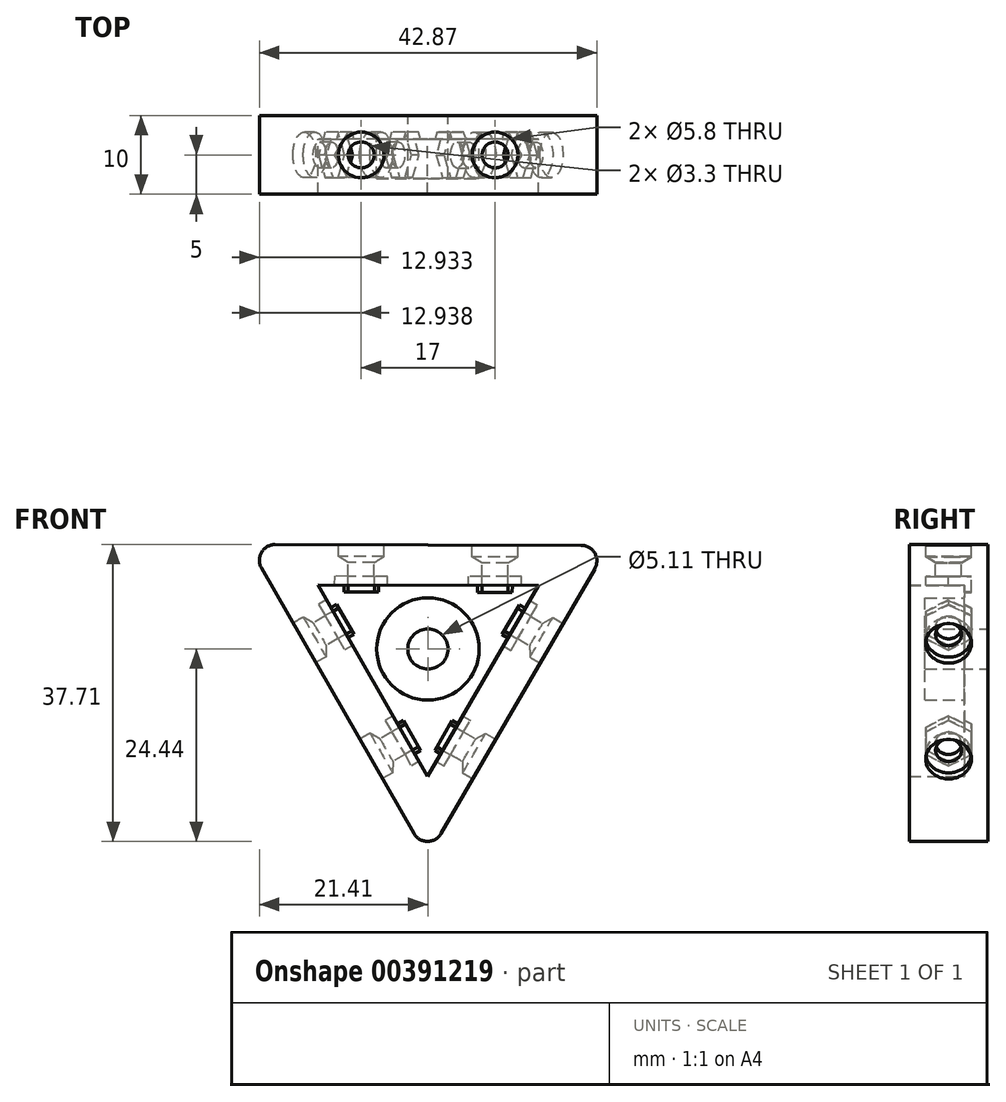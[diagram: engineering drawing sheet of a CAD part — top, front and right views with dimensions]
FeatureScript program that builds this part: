
annotation { "Feature Type Name" : "Feature", "Feature Type Description" : "" }
export const myFeature = defineFeature(function(context is Context, id is Id, definition is map)
    precondition{}
    {
        {
            var Q0;
            Q0=qCreatedBy(makeId("Front.planeOp"),FACE);
            var sketch = newSketch(context, id + "F0", { "sketchPlane" : qUnion([Q0])});
            skCircle(sketch, "E0.cCircle", {"center": v(0, 0) * mm, "radius": 13.22 * mm, "construction": true});
            skLineSegment(sketch, "E0.0", {"start": v(22.93, 13.17) * mm, "end": v(-0.06, -26.44) * mm});
            skLineSegment(sketch, "E0.1", {"start": v(-0.06, -26.44) * mm, "end": v(-22.87, 13.27) * mm});
            skLineSegment(sketch, "E0.2", {"start": v(-22.87, 13.27) * mm, "end": v(22.93, 13.17) * mm});
            skCircle(sketch, "E1.cCircle", {"center": v(0, 0) * mm, "radius": 8.08 * mm, "construction": true});
            skLineSegment(sketch, "E1.0", {"start": v(14.02, 8.05) * mm, "end": v(-0.04, -16.17) * mm});
            skLineSegment(sketch, "E1.1", {"start": v(-0.04, -16.17) * mm, "end": v(-13.98, 8.11) * mm});
            skLineSegment(sketch, "E1.2", {"start": v(-13.98, 8.11) * mm, "end": v(14.02, 8.05) * mm});
            skPoint(sketch, "E1.0.midPoint", {"position": v(7, -4.06) * mm});
            skPoint(sketch, "E2", {"position": v(2.72, -11.4) * mm});
            skPoint(sketch, "E3", {"position": v(11.26, 3.3) * mm});
            skPoint(sketch, "E4", {"position": v(8.52, 8.06) * mm});
            skPoint(sketch, "E5", {"position": v(-8.48, 8.1) * mm});
            skPoint(sketch, "E6", {"position": v(-10.82, 2.61) * mm});
            skPoint(sketch, "E7", {"position": v(-2.78, -11.4) * mm});
            skCircle(sketch, "E8", {"center": v(0, 0) * mm, "radius": 6.5 * mm});
            skSolve(sketch);
        }
        {
            var Q0;
            Q0=makeQuery(id+"F0.imprint","IMPRINT",FACE,{"disambiguationData":[TD([[makeQuery(id+"F0.imprint","IMPRINT",EDGE,{"derivedFrom":sQuery(id+"F0.wireOp",EDGE,"E1.0")}),-1.0]])]});
            extrude(context, id + "F1", {"entities" : qUnion([Q0]), "depth" : 3 * mm});
        }
        {
            var Q0;
            Q0=makeQuery(id+"F0.imprint","IMPRINT",FACE,{"disambiguationData":[TD([[makeQuery(id+"F0.imprint","IMPRINT",EDGE,{"derivedFrom":sQuery(id+"F0.wireOp",EDGE,"E0.0")}),-1.0]])]});
            extrude(context, id + "F2", {"entities" : qUnion([Q0]), "operationType" : NewBodyOperationType.ADD, "depth" : 10 * mm});
        }
        {
            var Q0;
            Q0=makeQuery(id+"F2.opExtrude","SWEPT_FACE",FACE,{"disambiguationData":[OSD([sQuery(id+"F0.wireOp",EDGE,"E0.0")])]});
            var sketch = newSketch(context, id + "F3", { "sketchPlane" : qUnion([Q0])});
            skPoint(sketch, "E9", {"position": v(-5, -8.5) * mm});
            skPoint(sketch, "E10", {"position": v(-5, 8.5) * mm});
            skPoint(sketch, "E10.positionSnap0", {"position": v(-5, 22.9) * mm});
            skCircle(sketch, "E11.cCircle", {"center": v(-5, -8.5) * mm, "radius": 2.9 * mm, "construction": true});
            skLineSegment(sketch, "E11.0", {"start": v(-2.1, -6.83) * mm, "end": v(-2.1, -10.17) * mm});
            skLineSegment(sketch, "E11.1", {"start": v(-2.1, -10.17) * mm, "end": v(-5, -11.85) * mm});
            skLineSegment(sketch, "E11.2", {"start": v(-5, -11.85) * mm, "end": v(-7.9, -10.17) * mm});
            skLineSegment(sketch, "E11.3", {"start": v(-7.9, -10.17) * mm, "end": v(-7.9, -6.83) * mm});
            skLineSegment(sketch, "E11.4", {"start": v(-7.9, -6.83) * mm, "end": v(-5, -5.15) * mm});
            skLineSegment(sketch, "E11.5", {"start": v(-5, -5.15) * mm, "end": v(-2.1, -6.83) * mm});
            skPoint(sketch, "E11.0.midPoint", {"position": v(-2.1, -8.5) * mm});
            skCircle(sketch, "E12.cCircle", {"center": v(-5, 8.5) * mm, "radius": 2.9 * mm, "construction": true});
            skLineSegment(sketch, "E12.0", {"start": v(-2.1, 10.17) * mm, "end": v(-2.1, 6.83) * mm});
            skLineSegment(sketch, "E12.1", {"start": v(-2.1, 6.83) * mm, "end": v(-5, 5.15) * mm});
            skLineSegment(sketch, "E12.2", {"start": v(-5, 5.15) * mm, "end": v(-7.9, 6.83) * mm});
            skLineSegment(sketch, "E12.3", {"start": v(-7.9, 6.83) * mm, "end": v(-7.9, 10.17) * mm});
            skLineSegment(sketch, "E12.4", {"start": v(-7.9, 10.17) * mm, "end": v(-5, 11.85) * mm});
            skLineSegment(sketch, "E12.5", {"start": v(-5, 11.85) * mm, "end": v(-2.1, 10.17) * mm});
            skPoint(sketch, "E12.0.midPoint", {"position": v(-2.1, 8.5) * mm});
            skSolve(sketch);
        }
        {
            var Q0;
            Q0=sQuery(id+"F3.wireOp",VERTEX,"E9");
            var Q1;
            Q1=sQuery(id+"F3.wireOp",VERTEX,"E10");
            var Q2;
            Q2=makeQuery(id+"F1.opExtrude","SWEPT_BODY",BODY,{"disambiguationData":[OSD([sQuery(id+"F0.wireOp",EDGE,"E1.0"),sQuery(id+"F0.wireOp",EDGE,"E1.1"),sQuery(id+"F0.wireOp",EDGE,"E1.2")])]});
            hole(context, id + "F4", {"style" : HoleStyle.SIMPLE, "endStyle" : HoleEndStyle.BLIND, "standardTappedOrClearance" : lookupTablePath({ "standard" : "ISO", "fit" : "Normal", "size" : "M3", "type" : "Clearance" }), "standardBlindInLast" : lookupTablePath({ "fit" : "Standard", "standard" : "ISO", "size" : "M3", "type" : "Clearance" }), "holeDiameter" : 3.3 * mm, "holeDepth" : 8 * mm, "tappedDepth" : 12 * mm, "tapClearance" : 3, "locations" : qUnion([Q0, Q1]), "scope" : qUnion([Q2])});
        }
        {
            var Q0;
            Q0=sQuery(id+"F3.wireOp",VERTEX,"E9");
            var Q1;
            Q1=sQuery(id+"F3.wireOp",VERTEX,"E10");
            var Q2;
            Q2=makeQuery(id+"F1.opExtrude","SWEPT_BODY",BODY,{"disambiguationData":[OSD([sQuery(id+"F0.wireOp",EDGE,"E1.0"),sQuery(id+"F0.wireOp",EDGE,"E1.1"),sQuery(id+"F0.wireOp",EDGE,"E1.2")])]});
            hole(context, id + "F5", {"style" : HoleStyle.SIMPLE, "endStyle" : HoleEndStyle.BLIND, "holeDiameter" : 5.8 * mm, "holeDepth" : 1.5 * mm, "tappedDepth" : 12 * mm, "tapClearance" : 3, "locations" : qUnion([Q0, Q1]), "scope" : qUnion([Q2])});
        }
        {
            var Q0;
            Q0=qSketchRegion(id+"F3",true);
            extrude(context, id + "F6", {"entities" : qUnion([Q0]), "operationType" : NewBodyOperationType.REMOVE, "oppositeDirection" : true, "depth" : 6 * mm, "hasSecondDirection" : true, "secondDirectionOppositeDirection" : true, "secondDirectionDepth" : 4 * mm});
        }
        {
            var Q0;
            Q0=makeQuery(id+"F2.opExtrude","SWEPT_FACE",FACE,{"disambiguationData":[OSD([sQuery(id+"F0.wireOp",EDGE,"E0.2")])]});
            var sketch = newSketch(context, id + "F7", { "sketchPlane" : qUnion([Q0])});
            skPoint(sketch, "E13", {"position": v(22.9, -5) * mm});
            skPoint(sketch, "E14", {"position": v(8.5, -5) * mm});
            skPoint(sketch, "E15", {"position": v(-8.5, -5) * mm});
            skPoint(sketch, "E15.positionSnap0", {"position": v(-22.9, -5) * mm});
            skCircle(sketch, "E16.cCircle", {"center": v(8.5, -5) * mm, "radius": 2.9 * mm, "construction": true});
            skLineSegment(sketch, "E16.0", {"start": v(5.15, -5) * mm, "end": v(6.83, -2.1) * mm});
            skLineSegment(sketch, "E16.1", {"start": v(6.83, -2.1) * mm, "end": v(10.17, -2.1) * mm});
            skLineSegment(sketch, "E16.2", {"start": v(10.17, -2.1) * mm, "end": v(11.85, -5) * mm});
            skLineSegment(sketch, "E16.3", {"start": v(11.85, -5) * mm, "end": v(10.17, -7.9) * mm});
            skLineSegment(sketch, "E16.4", {"start": v(10.17, -7.9) * mm, "end": v(6.83, -7.9) * mm});
            skLineSegment(sketch, "E16.5", {"start": v(6.83, -7.9) * mm, "end": v(5.15, -5) * mm});
            skPoint(sketch, "E16.0.midPoint", {"position": v(5.99, -3.55) * mm});
            skCircle(sketch, "E17.cCircle", {"center": v(-8.5, -5) * mm, "radius": 2.9 * mm, "construction": true});
            skLineSegment(sketch, "E17.0", {"start": v(-11.85, -5) * mm, "end": v(-10.17, -2.1) * mm});
            skLineSegment(sketch, "E17.1", {"start": v(-10.17, -2.1) * mm, "end": v(-6.83, -2.1) * mm});
            skLineSegment(sketch, "E17.2", {"start": v(-6.83, -2.1) * mm, "end": v(-5.15, -5) * mm});
            skLineSegment(sketch, "E17.3", {"start": v(-5.15, -5) * mm, "end": v(-6.83, -7.9) * mm});
            skLineSegment(sketch, "E17.4", {"start": v(-6.83, -7.9) * mm, "end": v(-10.17, -7.9) * mm});
            skLineSegment(sketch, "E17.5", {"start": v(-10.17, -7.9) * mm, "end": v(-11.85, -5) * mm});
            skPoint(sketch, "E17.0.midPoint", {"position": v(-11.01, -3.55) * mm});
            skSolve(sketch);
        }
        {
            var Q0;
            Q0=qSketchRegion(id+"F7",true);
            extrude(context, id + "F8", {"entities" : qUnion([Q0]), "operationType" : NewBodyOperationType.REMOVE, "oppositeDirection" : true, "depth" : 6 * mm, "hasSecondDirection" : true, "secondDirectionOppositeDirection" : true, "secondDirectionDepth" : 4 * mm});
        }
        {
            var Q0;
            Q0=sQuery(id+"F7.wireOp",VERTEX,"E14");
            var Q1;
            Q1=sQuery(id+"F7.wireOp",VERTEX,"E15");
            var Q2;
            Q2=makeQuery(id+"F1.opExtrude","SWEPT_BODY",BODY,{"disambiguationData":[OSD([sQuery(id+"F0.wireOp",EDGE,"E1.0"),sQuery(id+"F0.wireOp",EDGE,"E1.1"),sQuery(id+"F0.wireOp",EDGE,"E1.2")])]});
            hole(context, id + "F9", {"style" : HoleStyle.SIMPLE, "endStyle" : HoleEndStyle.BLIND, "holeDiameter" : 5.8 * mm, "holeDepth" : 1.5 * mm, "tappedDepth" : 12 * mm, "tapClearance" : 3, "locations" : qUnion([Q0, Q1]), "scope" : qUnion([Q2])});
        }
        {
            var Q0;
            Q0=sQuery(id+"F7.wireOp",VERTEX,"E14");
            var Q1;
            Q1=sQuery(id+"F7.wireOp",VERTEX,"E15");
            var Q2;
            Q2=makeQuery(id+"F1.opExtrude","SWEPT_BODY",BODY,{"disambiguationData":[OSD([sQuery(id+"F0.wireOp",EDGE,"E1.0"),sQuery(id+"F0.wireOp",EDGE,"E1.1"),sQuery(id+"F0.wireOp",EDGE,"E1.2")])]});
            hole(context, id + "F10", {"style" : HoleStyle.SIMPLE, "endStyle" : HoleEndStyle.BLIND, "standardTappedOrClearance" : lookupTablePath({ "standard" : "ISO", "fit" : "Normal", "size" : "M3", "type" : "Clearance" }), "standardBlindInLast" : lookupTablePath({ "fit" : "Standard", "standard" : "ISO", "size" : "M3", "type" : "Clearance" }), "holeDiameter" : 3.3 * mm, "holeDepth" : 8 * mm, "tappedDepth" : 12 * mm, "tapClearance" : 3, "locations" : qUnion([Q0, Q1]), "scope" : qUnion([Q2])});
        }
        {
            var Q0;
            Q0=makeQuery(id+"F2.opExtrude","SWEPT_FACE",FACE,{"disambiguationData":[OSD([sQuery(id+"F0.wireOp",EDGE,"E0.1")])]});
            var sketch = newSketch(context, id + "F11", { "sketchPlane" : qUnion([Q0])});
            skPoint(sketch, "E18", {"position": v(5, 8.5) * mm});
            skPoint(sketch, "E18.positionSnap0", {"position": v(5, 22.9) * mm});
            skPoint(sketch, "E19", {"position": v(5, -8.5) * mm});
            skPoint(sketch, "E19.positionSnap0", {"position": v(5, -22.9) * mm});
            skCircle(sketch, "E20.cCircle", {"center": v(5, 8.5) * mm, "radius": 2.9 * mm, "construction": true});
            skLineSegment(sketch, "E20.0", {"start": v(5, 5.15) * mm, "end": v(2.1, 6.83) * mm});
            skLineSegment(sketch, "E20.1", {"start": v(2.1, 6.83) * mm, "end": v(2.1, 10.17) * mm});
            skLineSegment(sketch, "E20.2", {"start": v(2.1, 10.17) * mm, "end": v(5, 11.85) * mm});
            skLineSegment(sketch, "E20.3", {"start": v(5, 11.85) * mm, "end": v(7.9, 10.17) * mm});
            skLineSegment(sketch, "E20.4", {"start": v(7.9, 10.17) * mm, "end": v(7.9, 6.83) * mm});
            skLineSegment(sketch, "E20.5", {"start": v(7.9, 6.83) * mm, "end": v(5, 5.15) * mm});
            skPoint(sketch, "E20.0.midPoint", {"position": v(3.55, 5.99) * mm});
            skCircle(sketch, "E21.cCircle", {"center": v(5, -8.5) * mm, "radius": 2.9 * mm, "construction": true});
            skLineSegment(sketch, "E21.0", {"start": v(5, -11.85) * mm, "end": v(2.1, -10.17) * mm});
            skLineSegment(sketch, "E21.1", {"start": v(2.1, -10.17) * mm, "end": v(2.1, -6.83) * mm});
            skLineSegment(sketch, "E21.2", {"start": v(2.1, -6.83) * mm, "end": v(5, -5.15) * mm});
            skLineSegment(sketch, "E21.3", {"start": v(5, -5.15) * mm, "end": v(7.9, -6.83) * mm});
            skLineSegment(sketch, "E21.4", {"start": v(7.9, -6.83) * mm, "end": v(7.9, -10.17) * mm});
            skLineSegment(sketch, "E21.5", {"start": v(7.9, -10.17) * mm, "end": v(5, -11.85) * mm});
            skPoint(sketch, "E21.0.midPoint", {"position": v(3.55, -11.01) * mm});
            skSolve(sketch);
        }
        {
            var Q0;
            Q0=qSketchRegion(id+"F11",true);
            extrude(context, id + "F12", {"entities" : qUnion([Q0]), "operationType" : NewBodyOperationType.REMOVE, "oppositeDirection" : true, "depth" : 6 * mm, "hasSecondDirection" : true, "secondDirectionOppositeDirection" : true, "secondDirectionDepth" : 4 * mm});
        }
        {
            var Q0;
            Q0=sQuery(id+"F11.wireOp",VERTEX,"E18");
            var Q1;
            Q1=sQuery(id+"F11.wireOp",VERTEX,"E19");
            var Q2;
            Q2=makeQuery(id+"F1.opExtrude","SWEPT_BODY",BODY,{"disambiguationData":[OSD([sQuery(id+"F0.wireOp",EDGE,"E1.0"),sQuery(id+"F0.wireOp",EDGE,"E1.1"),sQuery(id+"F0.wireOp",EDGE,"E1.2")])]});
            hole(context, id + "F13", {"style" : HoleStyle.SIMPLE, "endStyle" : HoleEndStyle.BLIND, "standardTappedOrClearance" : lookupTablePath({ "standard" : "ISO", "fit" : "Normal", "size" : "M3", "type" : "Clearance" }), "standardBlindInLast" : lookupTablePath({ "fit" : "Standard", "standard" : "ISO", "size" : "M3", "type" : "Clearance" }), "holeDiameter" : 3.3 * mm, "holeDepth" : 8 * mm, "tappedDepth" : 12 * mm, "tapClearance" : 3, "locations" : qUnion([Q0, Q1]), "scope" : qUnion([Q2])});
        }
        {
            var Q0;
            Q0=sQuery(id+"F11.wireOp",VERTEX,"E18");
            var Q1;
            Q1=sQuery(id+"F11.wireOp",VERTEX,"E19");
            var Q2;
            Q2=makeQuery(id+"F1.opExtrude","SWEPT_BODY",BODY,{"disambiguationData":[OSD([sQuery(id+"F0.wireOp",EDGE,"E1.0"),sQuery(id+"F0.wireOp",EDGE,"E1.1"),sQuery(id+"F0.wireOp",EDGE,"E1.2")])]});
            hole(context, id + "F14", {"style" : HoleStyle.SIMPLE, "endStyle" : HoleEndStyle.BLIND, "holeDiameter" : 5.8 * mm, "holeDepth" : 1.5 * mm, "tappedDepth" : 12 * mm, "tapClearance" : 3, "locations" : qUnion([Q0, Q1]), "scope" : qUnion([Q2])});
        }
        {
            var Q0;
            Q0=makeQuery(id+"F2.opExtrude","SWEPT_EDGE",EDGE,{"disambiguationData":[OSD([sQuery(id+"F0.wireOp",EDGE,"E0.1"),sQuery(id+"F0.wireOp",EDGE,"E0.2")])]});
            var Q1;
            Q1=makeQuery(id+"F2.opExtrude","SWEPT_EDGE",EDGE,{"disambiguationData":[OSD([sQuery(id+"F0.wireOp",EDGE,"E0.0"),sQuery(id+"F0.wireOp",EDGE,"E0.1")])]});
            var Q2;
            Q2=makeQuery(id+"F2.opExtrude","SWEPT_EDGE",EDGE,{"disambiguationData":[OSD([sQuery(id+"F0.wireOp",EDGE,"E0.0"),sQuery(id+"F0.wireOp",EDGE,"E0.2")])]});
            fillet(context, id + "F15", {"entities" : qUnion([Q0, Q1, Q2]), "radius" : 2 * mm, "tangentPropagation" : true, "allowEdgeOverflow" : false});
        }
        {
            var Q0;
            Q0=makeQuery(id+"F0.imprint","IMPRINT",FACE,{"disambiguationData":[TD([[makeQuery(id+"F0.imprint","IMPRINT",EDGE,{"derivedFrom":sQuery(id+"F0.wireOp",EDGE,"E8")}),1.0]])]});
            extrude(context, id + "F16", {"entities" : qUnion([Q0]), "operationType" : NewBodyOperationType.ADD, "depth" : 8 * mm});
        }
        {
            var Q0;
            Q0=sQuery(id+"F0.wireOp",VERTEX,"E0.cCircle.center");
            var Q1;
            Q1=makeQuery(id+"F1.opExtrude","SWEPT_BODY",BODY,{"disambiguationData":[OSD([sQuery(id+"F0.wireOp",EDGE,"E1.0"),sQuery(id+"F0.wireOp",EDGE,"E1.1"),sQuery(id+"F0.wireOp",EDGE,"E1.2"),sQuery(id+"F0.wireOp",EDGE,"E8")])]});
            hole(context, id + "F17", {"style" : HoleStyle.SIMPLE, "endStyle" : HoleEndStyle.BLIND, "oppositeDirection" : true, "standardTappedOrClearance" : lookupTablePath({ "standard" : "ANSI", "engagement" : "75%", "pitch" : "20 tpi", "size" : "1/4", "type" : "Tapped" }), "standardBlindInLast" : lookupTablePath({ "standard" : "ANSI", "engagement" : "75%", "pitch" : "20 tpi", "size" : "1/4", "type" : "Tapped" }), "holeDiameter" : 5.1 * mm, "showTappedDepth" : true, "holeDepth" : 15.8 * mm, "tappedDepth" : 12 * mm, "tapClearance" : 3, "locations" : qUnion([Q0]), "scope" : qUnion([Q1]), "majorDiameter" : 6.35 * mm});
        }
    });
